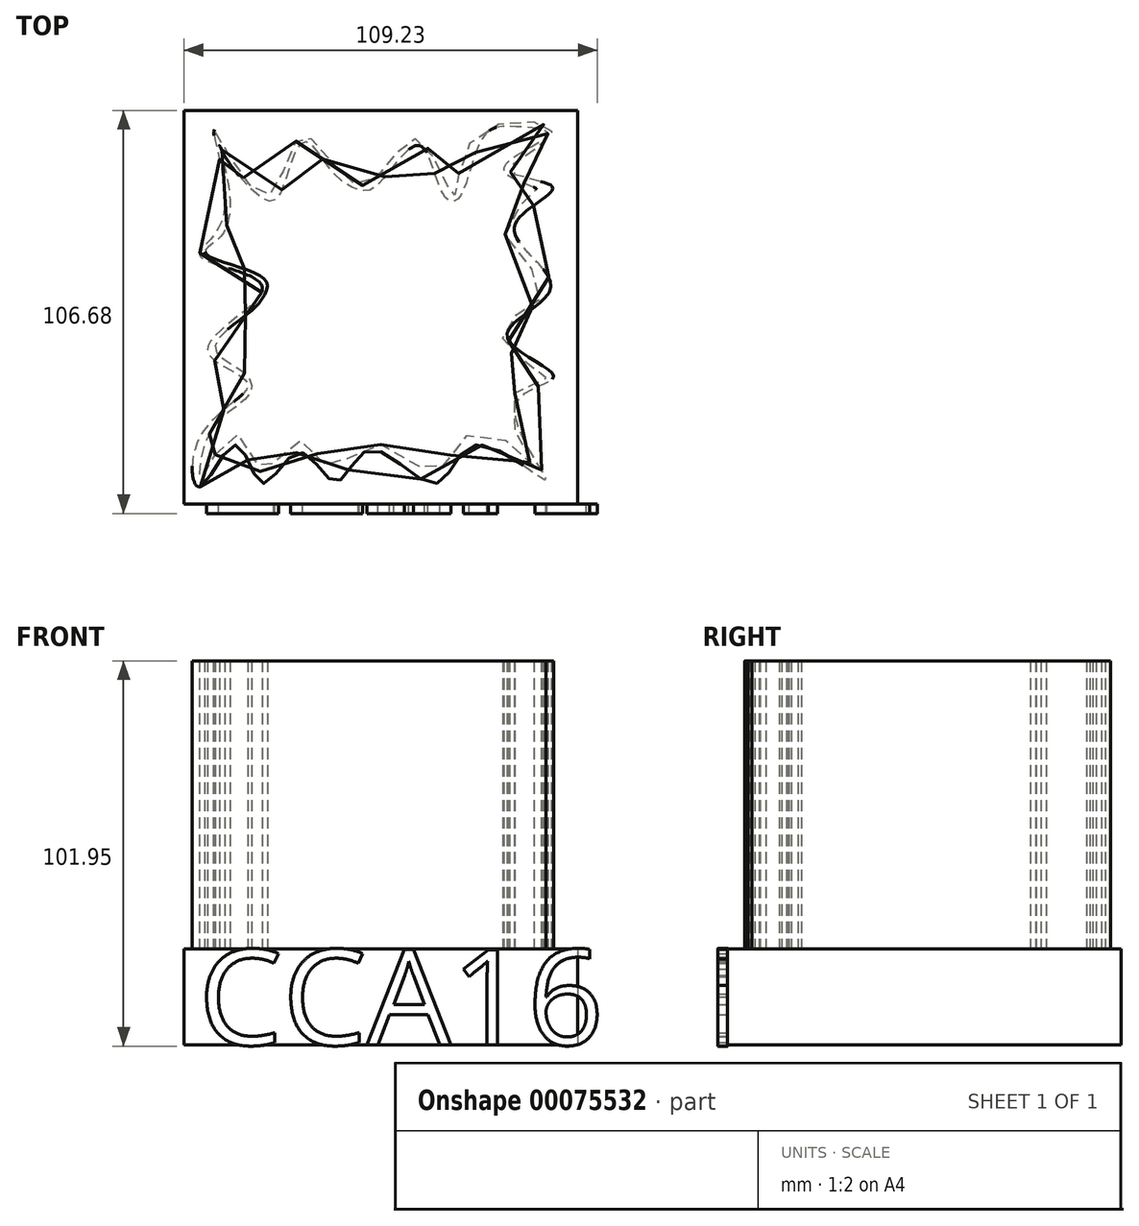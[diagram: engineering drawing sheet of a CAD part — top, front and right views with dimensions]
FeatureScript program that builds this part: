
annotation { "Feature Type Name" : "Feature", "Feature Type Description" : "" }
export const myFeature = defineFeature(function(context is Context, id is Id, definition is map)
    precondition{}
    {
        {
            var Q0;
            Q0=qCreatedBy(makeId("Top.planeOp"),FACE);
            var sketch = newSketch(context, id + "F0", { "sketchPlane" : qUnion([Q0])});
            skLineSegment(sketch, "E0.rect.bottom", {"start": v(-52.07, 52.07) * mm, "end": v(52.07, 52.07) * mm});
            skLineSegment(sketch, "E0.rect.top", {"start": v(-52.07, -52.07) * mm, "end": v(52.07, -52.07) * mm});
            skLineSegment(sketch, "E0.rect.left", {"start": v(-52.07, 52.07) * mm, "end": v(-52.07, -52.07) * mm});
            skLineSegment(sketch, "E0.rect.right", {"start": v(52.07, 52.07) * mm, "end": v(52.07, -52.07) * mm});
            skPoint(sketch, "E0.rect.middle", {"position": v(0, 0) * mm});
            skSolve(sketch);
        }
        {
            var Q0;
            Q0 = qSketchRegion(id + "F0", true);
            extrude(context, id + "F1", {"entities" : qUnion([Q0]), "depth" : 25.4 * mm});
        }
        {
            var Q0;
            Q0=makeQuery(id+"F1.opExtrude","CAP_FACE",FACE,{"disambiguationData":[OSD([sQuery(id+"F0.wireOp",EDGE,"E0.rect.bottom"),sQuery(id+"F0.wireOp",EDGE,"E0.rect.top"),sQuery(id+"F0.wireOp",EDGE,"E0.rect.left"),sQuery(id+"F0.wireOp",EDGE,"E0.rect.right")])],"isStart":false});
            var sketch = newSketch(context, id + "F2", { "sketchPlane" : qUnion([Q0])});
            skFitSpline(sketch, "E1", {"points": [v(-47.84, -47.49) * mm, v(-38.31, -36.46) * mm, v(-31.4, -46.65) * mm, v(-21.68, -38.38) * mm, v(-12.04, -46.22) * mm, v(-3.05, -37.8) * mm, v(14.42, -46.7) * mm, v(25.1, -36.48) * mm, v(43.64, -45.6) * mm, v(35.65, -25.87) * mm, v(45.61, -18.23) * mm, v(33.33, -7.7) * mm, v(44.96, 5.4) * mm, v(35.25, 21.23) * mm, v(45.41, 31.73) * mm, v(33.98, 36.26) * mm, v(45.33, 46.13) * mm, v(25.14, 45.3) * mm, v(19.14, 29.45) * mm, v(9.27, 44.52) * mm, v(-5.19, 32.2) * mm, v(-20.86, 45.37) * mm, v(-30.42, 29.5) * mm, v(-44.15, 46.74) * mm, v(-41.91, 23.54) * mm, v(-47.72, 13.3) * mm, v(-31.4, 5.22) * mm, v(-45.93, -11.17) * mm, v(-35.36, -19.98) * mm, v(-47.71, -33.91) * mm, v(-47.84, -47.49) * mm]});
            skFitSpline(sketch, "E2", {"points": [v(-43.88, -38.96) * mm, v(-38.31, -33.54) * mm, v(-32.73, -41.4) * mm, v(-31.4, -43.72) * mm, v(-24.13, -36.46) * mm, v(-18.74, -36.46) * mm, v(-12.38, -43.45) * mm, v(-5.57, -36.46) * mm, v(7.36, -40.2) * mm, v(14.42, -43.6) * mm, v(20.3, -36.46) * mm, v(29.42, -33.1) * mm, v(40.42, -41.98) * mm, v(34.69, -30.66) * mm, v(36.47, -21.86) * mm, v(43.92, -18.32) * mm, v(36.18, -13.3) * mm, v(32.15, -8.31) * mm, v(34.95, -2.59) * mm, v(39.71, 0) * mm, v(42.78, 5.4) * mm, v(34.42, 16.25) * mm, v(33.9, 24.92) * mm, v(42.33, 30.3) * mm, v(33.33, 34.97) * mm, v(33.9, 38.75) * mm, v(44.1, 45.84) * mm, v(35.56, 47.78) * mm, v(27.11, 45.16) * mm, v(20.5, 28.85) * mm, v(17.11, 28.95) * mm, v(12.35, 40.4) * mm, v(9.05, 42.73) * mm, v(1.19, 34.77) * mm, v(-3.96, 30.8) * mm, v(-12.21, 35.06) * mm, v(-18.43, 43.03) * mm, v(-21.34, 43.22) * mm, v(-26.39, 30.7) * mm, v(-29.88, 28.07) * mm, v(-40.95, 39.43) * mm, v(-42.78, 42.85) * mm, v(-40.06, 29.7) * mm, v(-43.04, 18.03) * mm, v(-46.6, 14.53) * mm, v(-35.97, 10.06) * mm, v(-30.08, 5.97) * mm, v(-32.54, 0.79) * mm, v(-37.7, -3.59) * mm, v(-43.87, -11.17) * mm, v(-35.67, -17.76) * mm, v(-34.82, -23.02) * mm, v(-43.14, -30.24) * mm, v(-47.71, -40.51) * mm, v(-47.71, -44.92) * mm, v(-43.88, -38.96) * mm]});
            skSolve(sketch);
        }
        {
            var Q0;
            Q0 = qSketchRegion(id + "F2", true);
            extrude(context, id + "F3", {"entities" : qUnion([Q0]), "operationType" : NewBodyOperationType.ADD, "depth" : 76.2 * mm});
        }
        {
            var Q0;
            Q0=makeQuery(id+"F1.opExtrude","SWEPT_FACE",FACE,{"disambiguationData":[OSD([sQuery(id+"F0.wireOp",EDGE,"E0.rect.top")])]});
            var sketch = newSketch(context, id + "F4", { "sketchPlane" : qUnion([Q0])});
            skText(sketch, "E3", { "text": "CCA16\n", "fontName": "OpenSans-Regular.ttf"});
            const initialGuessF4  = {"E3": [-0.0483, 0, 1, 0, 0.0254]};
            skSetInitialGuess(sketch, initialGuessF4);
            skSolve(sketch);
        }
        {
            var Q0;
            Q0 = qSketchRegion(id + "F4", true);
            extrude(context, id + "F5", {"entities" : qUnion([Q0]), "operationType" : NewBodyOperationType.ADD, "depth" : 2.54 * mm});
        }
    });
